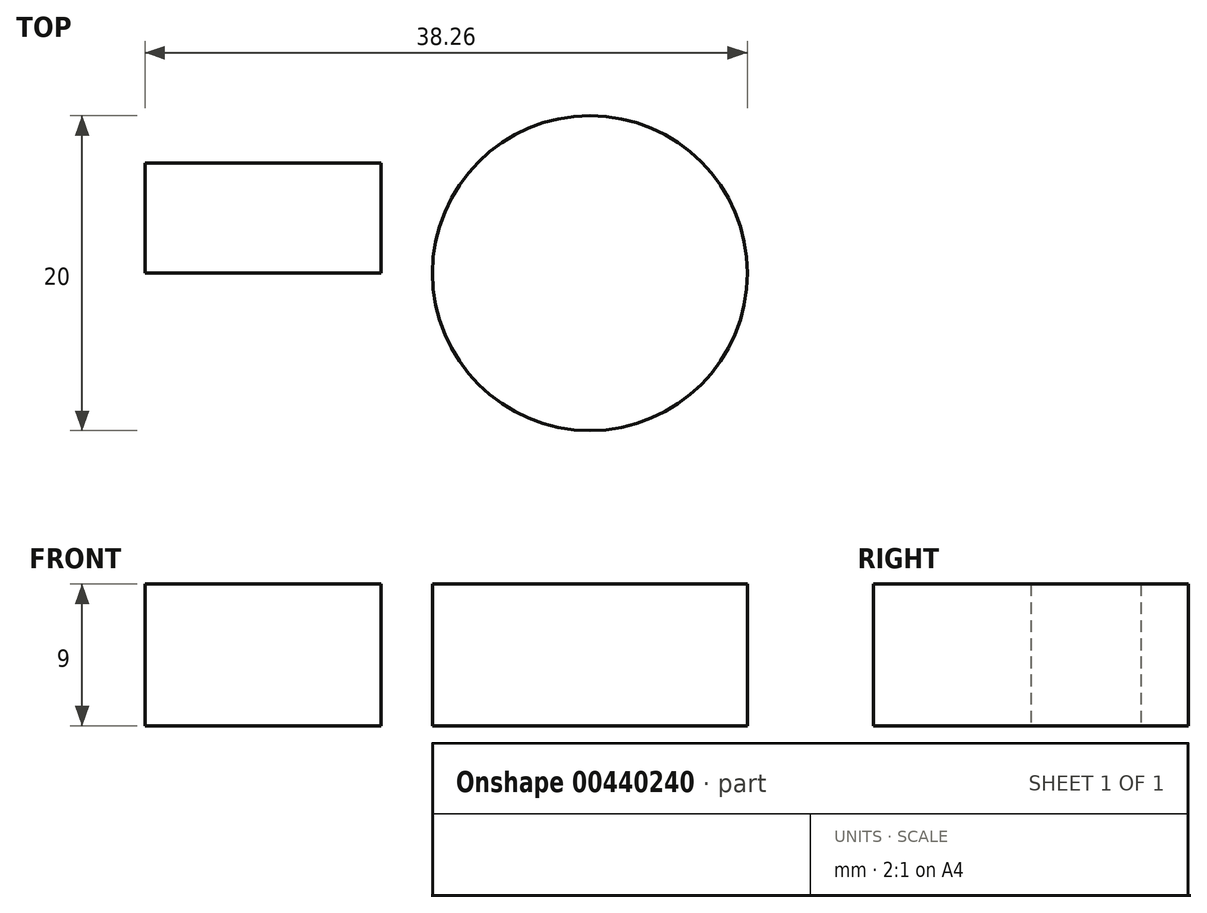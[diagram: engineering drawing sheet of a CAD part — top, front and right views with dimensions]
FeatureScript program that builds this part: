
annotation { "Feature Type Name" : "Feature", "Feature Type Description" : "" }
export const myFeature = defineFeature(function(context is Context, id is Id, definition is map)
    precondition{}
    {
        {
            var Q0;
            Q0=qCreatedBy(makeId("Top.planeOp"),FACE);
            var sketch = newSketch(context, id + "F0", { "sketchPlane" : qUnion([Q0])});
            skLineSegment(sketch, "E0.bottom", {"start": v(0, 0) * mm, "end": v(15, 0) * mm});
            skLineSegment(sketch, "E0.top", {"start": v(0, 7) * mm, "end": v(15, 7) * mm});
            skLineSegment(sketch, "E0.left", {"start": v(0, 0) * mm, "end": v(0, 7) * mm});
            skLineSegment(sketch, "E0.right", {"start": v(15, 0) * mm, "end": v(15, 7) * mm});
            skCircle(sketch, "E1", {"center": v(28.26, 0) * mm, "radius": 10 * mm});
            skSolve(sketch);
        }
        {
            var Q0;
            Q0=makeQuery(id+"F0.imprint","IMPRINT",FACE,{"disambiguationData":[TD([[makeQuery(id+"F0.imprint","IMPRINT",EDGE,{"derivedFrom":sQuery(id+"F0.wireOp",EDGE,"E0.bottom")}),1.0]])]});
            var Q1;
            Q1=makeQuery(id+"F0.imprint","IMPRINT",FACE,{"disambiguationData":[TD([[makeQuery(id+"F0.imprint","IMPRINT",EDGE,{"derivedFrom":sQuery(id+"F0.wireOp",EDGE,"E1")}),1.0]])]});
            extrude(context, id + "F1", {"entities" : qUnion([Q0, Q1]), "endBound" : BoundingType.SYMMETRIC, "depth" : 9 * mm});
        }
    });
